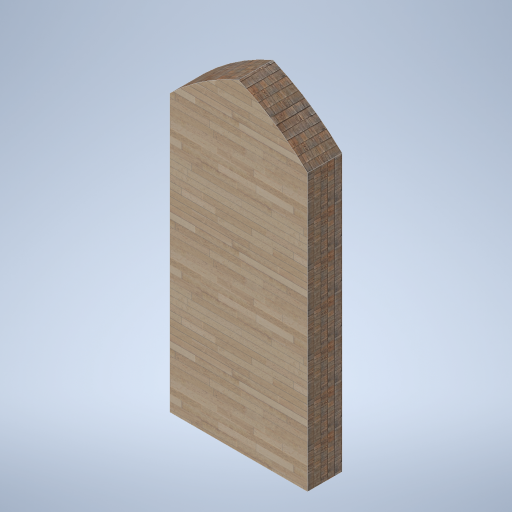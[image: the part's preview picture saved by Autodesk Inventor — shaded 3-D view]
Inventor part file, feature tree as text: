
AUTODESK INVENTOR PART (.ipt)
format: ipt  version: 2024.2 (Build 282272000, 272)  size: 409,088 bytes
history: native  units: in
note: dims shown in document units (in); Inventor stores cm internally (conversion verified against a paired STEP export)
features: sketch x7, other x3
ambient origin geometry x8: Origin, YZ Plane, XZ Plane, XY Plane, X Axis, Y Axis, Z Axis, Center Point
bodies: Solid1 (feature_tree)
feature tree (10):
  other  "door.ipt"
  other  "Solid1::door.ipt"
  other  "TaggingFeature1"
  sketch  "Sketch1"  dims[d0=0.3937in]
  sketch  "Sketch2"
  sketch  "草圖3"
  sketch  "草圖4"
  sketch  "草圖5"
  sketch  "草圖6"
  sketch  "草圖7"
